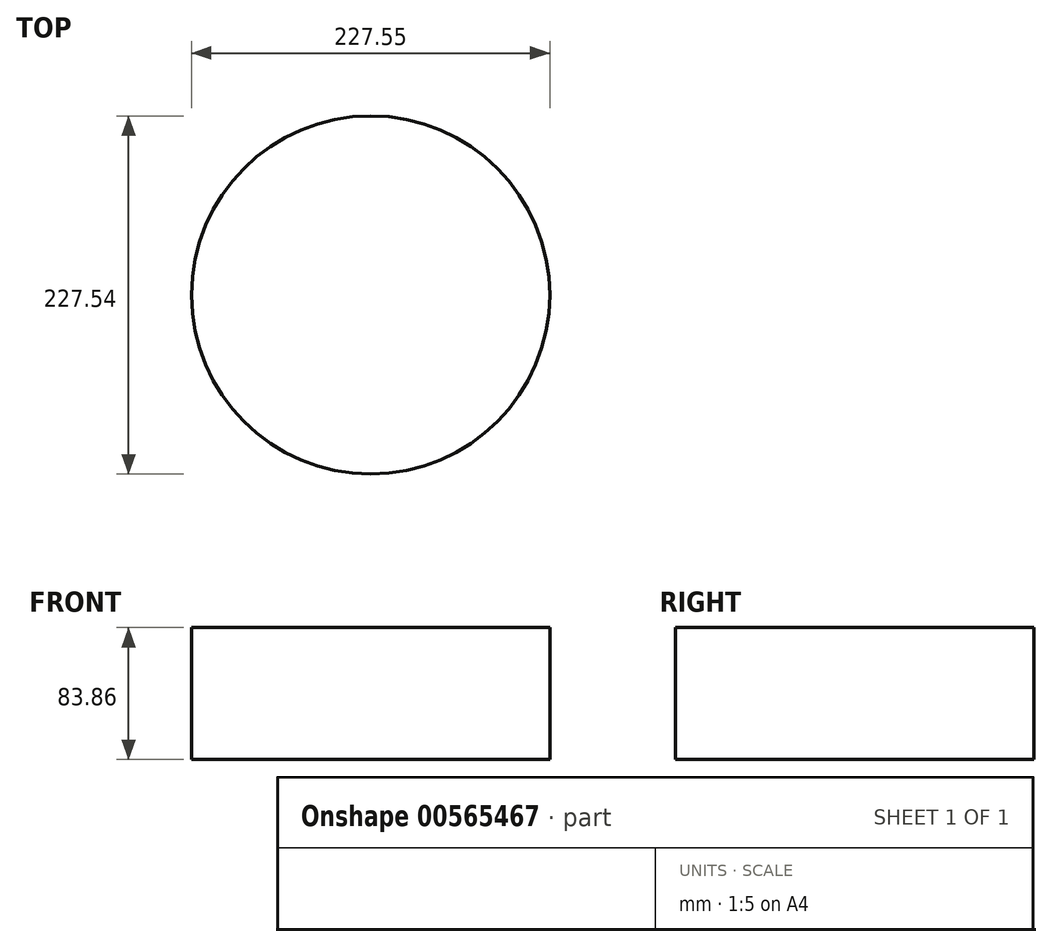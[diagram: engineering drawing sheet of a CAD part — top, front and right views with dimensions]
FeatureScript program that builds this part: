
annotation { "Feature Type Name" : "Feature", "Feature Type Description" : "" }
export const myFeature = defineFeature(function(context is Context, id is Id, definition is map)
    precondition{}
    {
        {
            var Q0;
            Q0=qCreatedBy(makeId("Front.planeOp"),FACE);
            var sketch = newSketch(context, id + "F0", { "sketchPlane" : qUnion([Q0])});
            skLineSegment(sketch, "E0.bottom", {"start": v(56.89, -41.93) * mm, "end": v(-56.89, -41.93) * mm});
            skLineSegment(sketch, "E0.top", {"start": v(56.89, 41.93) * mm, "end": v(-56.89, 41.93) * mm});
            skLineSegment(sketch, "E0.left", {"start": v(56.89, -41.93) * mm, "end": v(56.89, 41.93) * mm});
            skLineSegment(sketch, "E0.right", {"start": v(-56.89, -41.93) * mm, "end": v(-56.89, 41.93) * mm});
            skPoint(sketch, "E0.middle", {"position": v(0, 0) * mm});
            skPoint(sketch, "E1.middle", {"position": v(17.83, 41.93) * mm});
            skSolve(sketch);
        }
        {
            var Q0;
            Q0=makeQuery(id+"F0.imprint","IMPRINT",FACE,{"disambiguationData":[TD([[makeQuery(id+"F0.imprint","IMPRINT",EDGE,{"derivedFrom":sQuery(id+"F0.wireOp",EDGE,"E0.bottom")}),-1.0]])]});
            var Q1;
            Q1=sQuery(id+"F0.wireOp",EDGE,"E0.left");
            revolve(context, id + "F1", {"entities" : qUnion([Q0]), "axis" : qUnion([Q1]), "revolveType" : RevolveType.FULL});
        }
    });
